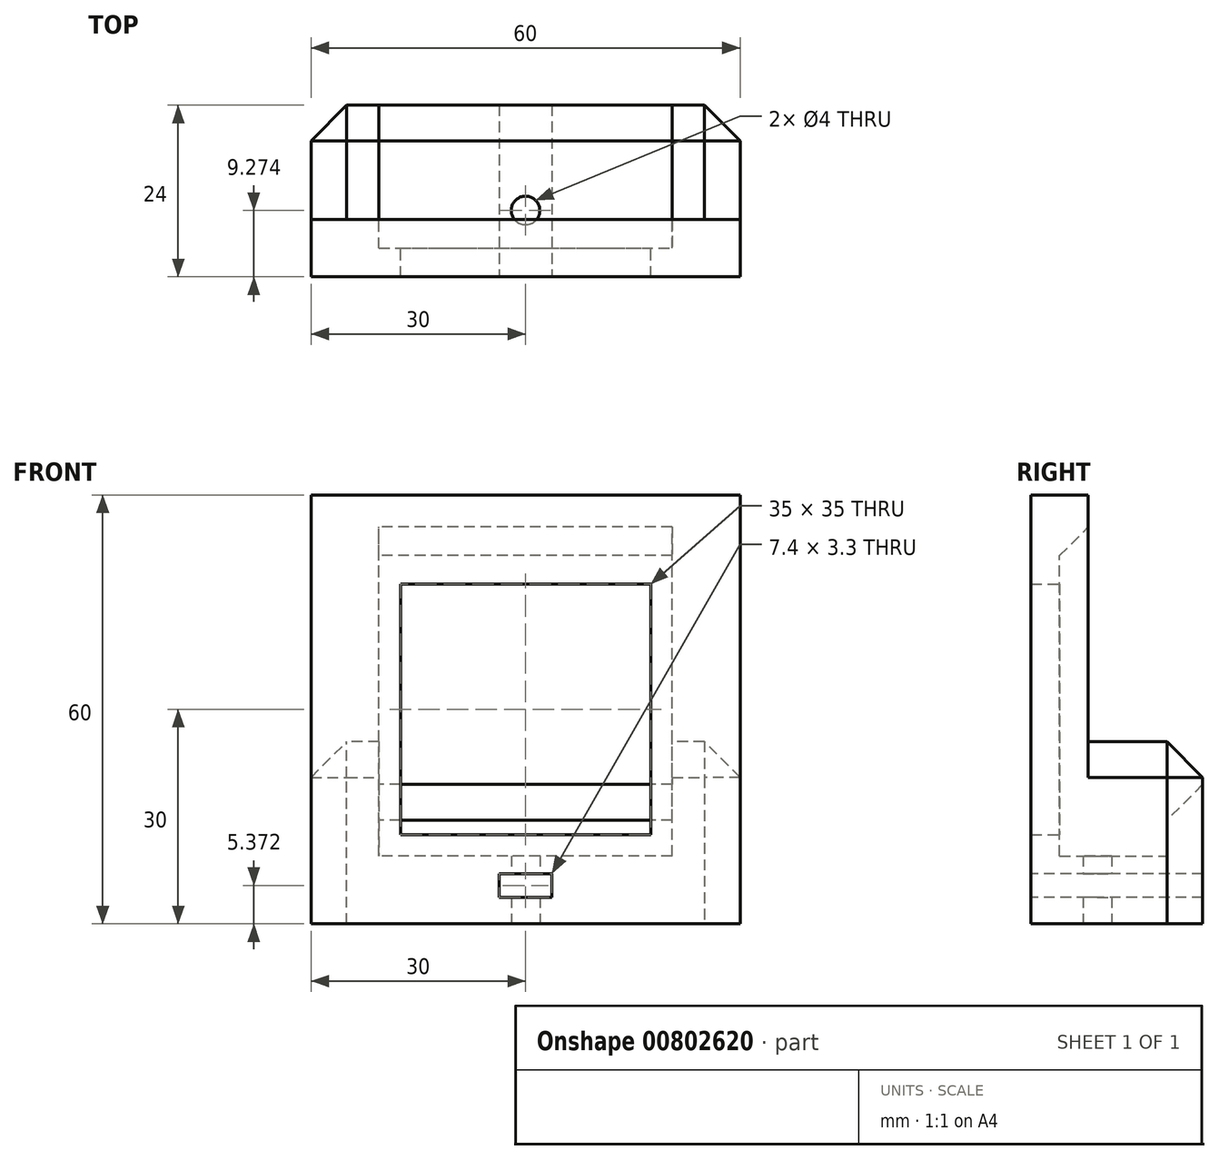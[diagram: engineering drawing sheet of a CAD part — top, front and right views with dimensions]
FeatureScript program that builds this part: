
annotation { "Feature Type Name" : "Feature", "Feature Type Description" : "" }
export const myFeature = defineFeature(function(context is Context, id is Id, definition is map)
    precondition{}
    {
        {
            var Q0;
            Q0=qCreatedBy(makeId("Front.planeOp"),FACE);
            var sketch = newSketch(context, id + "F0", { "sketchPlane" : qUnion([Q0])});
            skLineSegment(sketch, "E0.bottom", {"start": v(-30, -30) * mm, "end": v(30, -30) * mm});
            skLineSegment(sketch, "E0.top", {"start": v(-30, 30) * mm, "end": v(30, 30) * mm});
            skLineSegment(sketch, "E0.left", {"start": v(-30, -30) * mm, "end": v(-30, 30) * mm});
            skLineSegment(sketch, "E0.right", {"start": v(30, -30) * mm, "end": v(30, 30) * mm});
            skLineSegment(sketch, "E1.bottom", {"start": v(-20.5, -20.5) * mm, "end": v(20.5, -20.5) * mm});
            skLineSegment(sketch, "E1.top", {"start": v(-20.5, 20.5) * mm, "end": v(20.5, 20.5) * mm});
            skLineSegment(sketch, "E1.left", {"start": v(-20.5, -20.5) * mm, "end": v(-20.5, 20.5) * mm});
            skLineSegment(sketch, "E1.right", {"start": v(20.5, -20.5) * mm, "end": v(20.5, 20.5) * mm});
            skLineSegment(sketch, "E2.bottom", {"start": v(-17.5, 17.5) * mm, "end": v(17.5, 17.5) * mm});
            skLineSegment(sketch, "E2.top", {"start": v(-17.5, -17.5) * mm, "end": v(17.5, -17.5) * mm});
            skLineSegment(sketch, "E2.left", {"start": v(-17.5, 17.5) * mm, "end": v(-17.5, -17.5) * mm});
            skLineSegment(sketch, "E2.right", {"start": v(17.5, 17.5) * mm, "end": v(17.5, -17.5) * mm});
            skSolve(sketch);
        }
        {
            var Q0;
            Q0 = qSketchRegion(id + "F0", true);
            extrude(context, id + "F1", {"entities" : qUnion([Q0]), "endBound" : BoundingType.SYMMETRIC, "depth" : 8 * mm, "offsetDistance" : 25 * mm});
        }
        {
            var Q0;
            Q0=makeQuery(id+"F0.imprint","IMPRINT",FACE,{"disambiguationData":[TD([[makeQuery(id+"F0.imprint","IMPRINT",EDGE,{"derivedFrom":sQuery(id+"F0.wireOp",EDGE,"E1.bottom")}),1.0]])]});
            extrude(context, id + "F2", {"entities" : qUnion([Q0]), "operationType" : NewBodyOperationType.ADD, "depth" : 4 * mm, "offsetDistance" : 25 * mm});
        }
        {
            var Q0;
            Q0=makeQuery(id+"F1.opExtrude","CAP_FACE",FACE,{"disambiguationData":[OSD([sQuery(id+"F0.wireOp",EDGE,"E0.bottom"),sQuery(id+"F0.wireOp",EDGE,"E0.top"),sQuery(id+"F0.wireOp",EDGE,"E0.left"),sQuery(id+"F0.wireOp",EDGE,"E0.right"),sQuery(id+"F0.wireOp",EDGE,"E1.bottom"),sQuery(id+"F0.wireOp",EDGE,"E1.top"),sQuery(id+"F0.wireOp",EDGE,"E1.left"),sQuery(id+"F0.wireOp",EDGE,"E1.right")])],"isStart":true});
            var sketch = newSketch(context, id + "F3", { "sketchPlane" : qUnion([Q0])});
            skLineSegment(sketch, "E3", {"start": v(-30, -14.5) * mm, "end": v(-20.5, -14.5) * mm});
            skLineSegment(sketch, "E4", {"start": v(-20.5, -14.5) * mm, "end": v(-20.5, -20.5) * mm});
            skLineSegment(sketch, "E5", {"start": v(-20.5, -20.5) * mm, "end": v(20.5, -20.5) * mm});
            skLineSegment(sketch, "E6", {"start": v(20.5, -20.5) * mm, "end": v(20.5, -14.5) * mm});
            skLineSegment(sketch, "E7", {"start": v(20.5, -14.5) * mm, "end": v(30, -14.5) * mm});
            skLineSegment(sketch, "E8", {"start": v(30, -14.5) * mm, "end": v(30, -30) * mm});
            skLineSegment(sketch, "E9", {"start": v(30, -30) * mm, "end": v(-30, -30) * mm});
            skLineSegment(sketch, "E10", {"start": v(-30, -30) * mm, "end": v(-30, -14.5) * mm});
            skSolve(sketch);
        }
        {
            var Q0;
            Q0=makeQuery(id+"F3.imprint","IMPRINT",FACE,{"disambiguationData":[TD([[makeQuery(id+"F3.imprint","IMPRINT",EDGE,{"derivedFrom":sQuery(id+"F3.wireOp",EDGE,"E3")}),-1.0]])]});
            extrude(context, id + "F4", {"entities" : qUnion([Q0]), "operationType" : NewBodyOperationType.ADD, "depth" : 16 * mm, "offsetDistance" : 25 * mm});
        }
        {
            var Q0;
            Q0=makeQuery(id+"F4.boolean.opBoolean","MERGE",FACE,{"derivedFrom":[makeQuery(id+"F1.opExtrude","SWEPT_FACE",FACE,{"disambiguationData":[OSD([sQuery(id+"F0.wireOp",EDGE,"E1.bottom")])]}),makeQuery(id+"F4.opExtrude","SWEPT_FACE",FACE,{"disambiguationData":[OSD([sQuery(id+"F3.wireOp",EDGE,"E5")])]})]});
            var sketch = newSketch(context, id + "F5", { "sketchPlane" : qUnion([Q0])});
            skLineSegment(sketch, "E11.0", {"start": v(30, 20) * mm, "end": v(30, 4) * mm, "construction": true});
            skLineSegment(sketch, "E12.0", {"start": v(-30, 20) * mm, "end": v(-30, 4) * mm, "construction": true});
            skLineSegment(sketch, "E13.bottom", {"start": v(30, 20) * mm, "end": v(-30, 20) * mm});
            skLineSegment(sketch, "E13.top", {"start": v(30, 15) * mm, "end": v(-30, 15) * mm});
            skLineSegment(sketch, "E13.left", {"start": v(30, 20) * mm, "end": v(30, 15) * mm});
            skLineSegment(sketch, "E13.right", {"start": v(-30, 20) * mm, "end": v(-30, 15) * mm});
            skLineSegment(sketch, "E14.0", {"start": v(-20.5, 0) * mm, "end": v(20.5, 0) * mm, "construction": true});
            skSolve(sketch);
        }
        {
            var Q0;
            Q0 = qSketchRegion(id + "F5", true);
            var Q1;
            Q1=makeQuery(id+"F4.opExtrude","SWEPT_FACE",FACE,{"disambiguationData":[OSD([sQuery(id+"F3.wireOp",EDGE,"E3")])]});
            var Q2;
            Q2=makeQuery(id+"F4.opExtrude","SWEPT_FACE",FACE,{"disambiguationData":[OSD([sQuery(id+"F3.wireOp",EDGE,"E7")])]});
            extrude(context, id + "F6", {"entities" : qUnion([Q0, Q1, Q2]), "operationType" : NewBodyOperationType.ADD, "depth" : 10 * mm, "offsetDistance" : 25 * mm});
        }
        {
            var Q0;
            Q0=makeQuery(id+"F6.opExtrude","CAP_EDGE",EDGE,{"disambiguationData":[OSD([sQuery(id+"F5.wireOp",EDGE,"E13.top")])],"isStart":false});
            var Q1;
            {var subQ0=sQuery(id+"F3.wireOp",EDGE,"E3");Q1=makeQuery(id+"F6.opExtrude","CAP_EDGE",EDGE,{"disambiguationData":[OSD([subQ0]),TDD([makeQuery(id+"F4.opExtrude","CAP_EDGE",EDGE,{"disambiguationData":[OSD([subQ0])],"isStart":false})])],"isStart":false});}
            var Q2;
            {var subQ0=sQuery(id+"F3.wireOp",EDGE,"E7");Q2=makeQuery(id+"F6.opExtrude","CAP_EDGE",EDGE,{"disambiguationData":[OSD([subQ0]),TDD([makeQuery(id+"F4.opExtrude","CAP_EDGE",EDGE,{"disambiguationData":[OSD([subQ0])],"isStart":false})])],"isStart":false});}
            var Q3;
            {var subQ0=sQuery(id+"F3.wireOp",EDGE,"E7");Q3=makeQuery(id+"F6.opExtrude","CAP_EDGE",EDGE,{"disambiguationData":[OSD([subQ0]),TDD([makeQuery(id+"F4.opExtrude","CAP_EDGE",EDGE,{"disambiguationData":[OSD([subQ0])],"isStart":true})])],"isStart":false});}
            var Q4;
            {var subQ0=sQuery(id+"F3.wireOp",EDGE,"E3");Q4=makeQuery(id+"F6.opExtrude","CAP_EDGE",EDGE,{"disambiguationData":[OSD([subQ0]),TDD([makeQuery(id+"F4.opExtrude","CAP_EDGE",EDGE,{"disambiguationData":[OSD([subQ0])],"isStart":true})])],"isStart":false});}
            var Q5;
            Q5=makeQuery(id+"F6.opExtrude","CAP_EDGE",EDGE,{"disambiguationData":[OSD([sQuery(id+"F0.wireOp",EDGE,"E0.right"),sQuery(id+"F3.wireOp",EDGE,"E3"),sQuery(id+"F3.wireOp",EDGE,"E10")])],"isStart":false});
            var Q6;
            Q6=makeQuery(id+"F6.opExtrude","CAP_EDGE",EDGE,{"disambiguationData":[OSD([sQuery(id+"F0.wireOp",EDGE,"E0.left"),sQuery(id+"F3.wireOp",EDGE,"E7"),sQuery(id+"F3.wireOp",EDGE,"E8")])],"isStart":false});
            var Q7;
            {var subQ0=sQuery(id+"F3.wireOp",EDGE,"E8");var subQ1=sQuery(id+"F3.wireOp",EDGE,"E7");var subQ2=sQuery(id+"F0.wireOp",EDGE,"E0.left");Q7=makeQuery(id+"F6.boolean.opBoolean","MERGE",EDGE,{"derivedFrom":[makeQuery(id+"F4.opExtrude","CAP_EDGE",EDGE,{"disambiguationData":[OSD([subQ0])],"isStart":false}),makeQuery(id+"F6.opExtrude","SWEPT_EDGE",EDGE,{"disambiguationData":[OSD([subQ2,subQ1,subQ0]),TDD([makeQuery(id+"F4.opExtrude","CAP_VERTEX",VERTEX,{"disambiguationData":[OSD([subQ2,subQ1,subQ0])],"isStart":false})])]}),makeQuery(id+"F6.opExtrude","SWEPT_EDGE",EDGE,{"disambiguationData":[OSD([sQuery(id+"F5.wireOp",EDGE,"E13.bottom"),sQuery(id+"F5.wireOp",EDGE,"E13.right")])]})]});}
            var Q8;
            {var subQ0=sQuery(id+"F3.wireOp",EDGE,"E10");var subQ1=sQuery(id+"F3.wireOp",EDGE,"E3");var subQ2=sQuery(id+"F0.wireOp",EDGE,"E0.right");Q8=makeQuery(id+"F6.boolean.opBoolean","MERGE",EDGE,{"derivedFrom":[makeQuery(id+"F4.opExtrude","CAP_EDGE",EDGE,{"disambiguationData":[OSD([subQ0])],"isStart":false}),makeQuery(id+"F6.opExtrude","SWEPT_EDGE",EDGE,{"disambiguationData":[OSD([subQ2,subQ1,subQ0]),TDD([makeQuery(id+"F4.opExtrude","CAP_VERTEX",VERTEX,{"disambiguationData":[OSD([subQ2,subQ1,subQ0])],"isStart":false})])]}),makeQuery(id+"F6.opExtrude","SWEPT_EDGE",EDGE,{"disambiguationData":[OSD([sQuery(id+"F5.wireOp",EDGE,"E13.bottom"),sQuery(id+"F5.wireOp",EDGE,"E13.left")])]})]});}
            var Q9;
            Q9=makeQuery(id+"F1.opExtrude","CAP_EDGE",EDGE,{"disambiguationData":[OSD([sQuery(id+"F0.wireOp",EDGE,"E1.top")])],"isStart":true});
            chamfer(context, id + "F7", {"entities" : qUnion([Q0, Q1, Q2, Q3, Q4, Q5, Q6, Q7, Q8, Q9]), "width" : 5 * mm, "tangentPropagation" : true});
        }
        {
            var Q0;
            {var subQ0=sQuery(id+"F0.wireOp",EDGE,"E1.right");var subQ1=sQuery(id+"F0.wireOp",EDGE,"E1.left");var subQ2=sQuery(id+"F0.wireOp",EDGE,"E1.top");var subQ3=sQuery(id+"F0.wireOp",EDGE,"E1.bottom");Q0=makeQuery(id+"F2.boolean.opBoolean","MERGE",FACE,{"derivedFrom":[makeQuery(id+"F1.opExtrude","CAP_FACE",FACE,{"disambiguationData":[OSD([sQuery(id+"F0.wireOp",EDGE,"E0.bottom"),sQuery(id+"F0.wireOp",EDGE,"E0.top"),sQuery(id+"F0.wireOp",EDGE,"E0.left"),sQuery(id+"F0.wireOp",EDGE,"E0.right"),subQ3,subQ2,subQ1,subQ0])],"isStart":false}),makeQuery(id+"F2.opExtrude","CAP_FACE",FACE,{"disambiguationData":[OSD([subQ3,subQ2,subQ1,subQ0,sQuery(id+"F0.wireOp",EDGE,"E2.bottom"),sQuery(id+"F0.wireOp",EDGE,"E2.top"),sQuery(id+"F0.wireOp",EDGE,"E2.left"),sQuery(id+"F0.wireOp",EDGE,"E2.right")])],"isStart":false})]});}
            var sketch = newSketch(context, id + "F8", { "sketchPlane" : qUnion([Q0])});
            skLineSegment(sketch, "E15.bottom", {"start": v(3.7, -26.28) * mm, "end": v(-3.7, -26.28) * mm});
            skLineSegment(sketch, "E15.top", {"start": v(3.7, -22.98) * mm, "end": v(-3.7, -22.98) * mm});
            skLineSegment(sketch, "E15.left", {"start": v(3.7, -26.28) * mm, "end": v(3.7, -22.98) * mm});
            skLineSegment(sketch, "E15.right", {"start": v(-3.7, -26.28) * mm, "end": v(-3.7, -22.98) * mm});
            skSolve(sketch);
        }
        {
            var Q0;
            Q0=makeQuery(id+"F8.imprint","IMPRINT",FACE,{"disambiguationData":[TD([[makeQuery(id+"F8.imprint","IMPRINT",EDGE,{"derivedFrom":sQuery(id+"F8.wireOp",EDGE,"E15.bottom")}),-1.0]])]});
            extrude(context, id + "F9", {"entities" : qUnion([Q0]), "operationType" : NewBodyOperationType.REMOVE, "oppositeDirection" : true, "depth" : 25 * mm, "offsetDistance" : 25 * mm});
        }
        {
            var Q0;
            Q0=makeQuery(id+"F4.boolean.opBoolean","MERGE",FACE,{"derivedFrom":[makeQuery(id+"F1.opExtrude","SWEPT_FACE",FACE,{"disambiguationData":[OSD([sQuery(id+"F0.wireOp",EDGE,"E0.bottom")])]}),makeQuery(id+"F4.opExtrude","SWEPT_FACE",FACE,{"disambiguationData":[OSD([sQuery(id+"F3.wireOp",EDGE,"E9")])]})]});
            var sketch = newSketch(context, id + "F10", { "sketchPlane" : qUnion([Q0])});
            skCircle(sketch, "E16", {"center": v(0, -5.27) * mm, "radius": 2 * mm});
            skSolve(sketch);
        }
        {
            var Q0;
            Q0=makeQuery(id+"F10.imprint","IMPRINT",FACE,{"disambiguationData":[TD([[makeQuery(id+"F10.imprint","IMPRINT",EDGE,{"derivedFrom":sQuery(id+"F10.wireOp",EDGE,"E16")}),1.0]])]});
            extrude(context, id + "F11", {"entities" : qUnion([Q0]), "operationType" : NewBodyOperationType.REMOVE, "oppositeDirection" : true, "depth" : 25 * mm, "offsetDistance" : 25 * mm});
        }
    });
